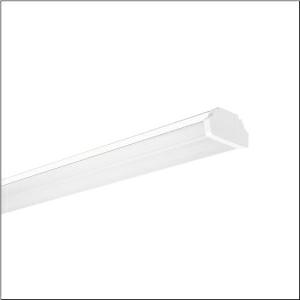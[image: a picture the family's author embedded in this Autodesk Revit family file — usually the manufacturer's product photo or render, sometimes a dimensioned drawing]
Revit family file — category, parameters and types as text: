
# Revit family: dus_31_gen_2_53bd812cv4a5d2_05be
name_source: partatom
category: Lighting Fixtures
units: mm (PartAtom-declared; Revit-internal decimal feet)

## family parameters
Cut with Voids When Loaded = No
Host = Face
Light Source = No
Part Type = Normal
Room Calculation Point = No
Round Connector Dimension = Use Diameter
Shared = No

## types (1)
- --- (1 x LED, 10570 lm, 54.8 W, 4000K)
    Apparent Load = 55 VA
    CIE Flux Codes = 47 80 95 93 100
    Color Rendering = 80
    Color Temperature = 4000K
    Default Elevation = 1800 mm
    Description = DUS 31 Gen.2, luminaire insert, of sheet steel, coil coated, white, length: 1.535mm, width: 81mm, height: 90mm, 5x system unit, system units: 307mm, LED rated luminous flux: 10.570lm, light colour: 840, SDCM (Standard Deviation of Colour Matching)MacAdam ≤ 3 SDCM (initial), control gear: ON/OFF Multilumen, CLOi, with plug, 3-pole, with phase selection, mains connection: 220..240V, AC, 50/60Hz, start of lifetime: 55W, end of service life: 65W, through-wiring accessed according to module size, primary optical cover: cover, of PMMA, light emission: direct distribution, primary light characteristic: symmetric, protection rating (complete): IP20, protection rating (LED compartment): IP50, insulation class (complete): insulation class I (protective earthing), certification: CE, ENEC, VDE, UKCA, impact resistance: IK03, permissible ambient temperature for indoor applications: -35..+40°C, corresponds to IFS (International Featured Standards) requirements for safety and quality in the food industry, reducing of maximum allowable ambient temperature of 5°C with ceiling mounting, packaging unit: 1 piece
    Height = 95 mm
    Lamp = 1 x LED
    Lamp Light Flux = 10570 lm
    Lamp Power = 54.8 W
    Lamp count = 1
    Length = 1535 mm
    Luminous efficacy = 193 lm/W
    Manufacturer = Siteco
    ModVariant = No
    Model = 53BD812CV4A5D2
    Mounting Place = Ceiling
    Mounting Type = Pendant
    Number of Poles = 1
    OnlyDefault = Yes
    Power Factor = 1
    Product Name = DUS 31 Gen.2
    Product group = luminaire insert | ceiling pendant
    ProductGroupID = 901
    Protection Class = Protection class I
    Protection Degree = IP 20
    RLX_Detail_Level = 1
    RLX_Emergency_Light_Flux = 0 lm
    RLX_Emergency_Type = 0
    RLX_Emergency_Type_DB = No
    RlxData = <blob elided: 29889 chars, md5=8567a84c>
    Socket = socket
    Standby Power = 0 W
    System Light Flux = 10570 lm
    System Power = 55 W
    Type Comments = factory setting: luminous flux: 100 % | (A | C | E) | 129 mA
    Type Image = l_1319596.jpg
    URL = http://relux.com
    VarID = @adj_042349
    Voltage = 0 V
    Weight = 0.00 kg
    Width = 81 mm

## geometry (parser evidence)
native form markers: Blend x4, Sweep x12
no freeform markers — native parametric forms only
